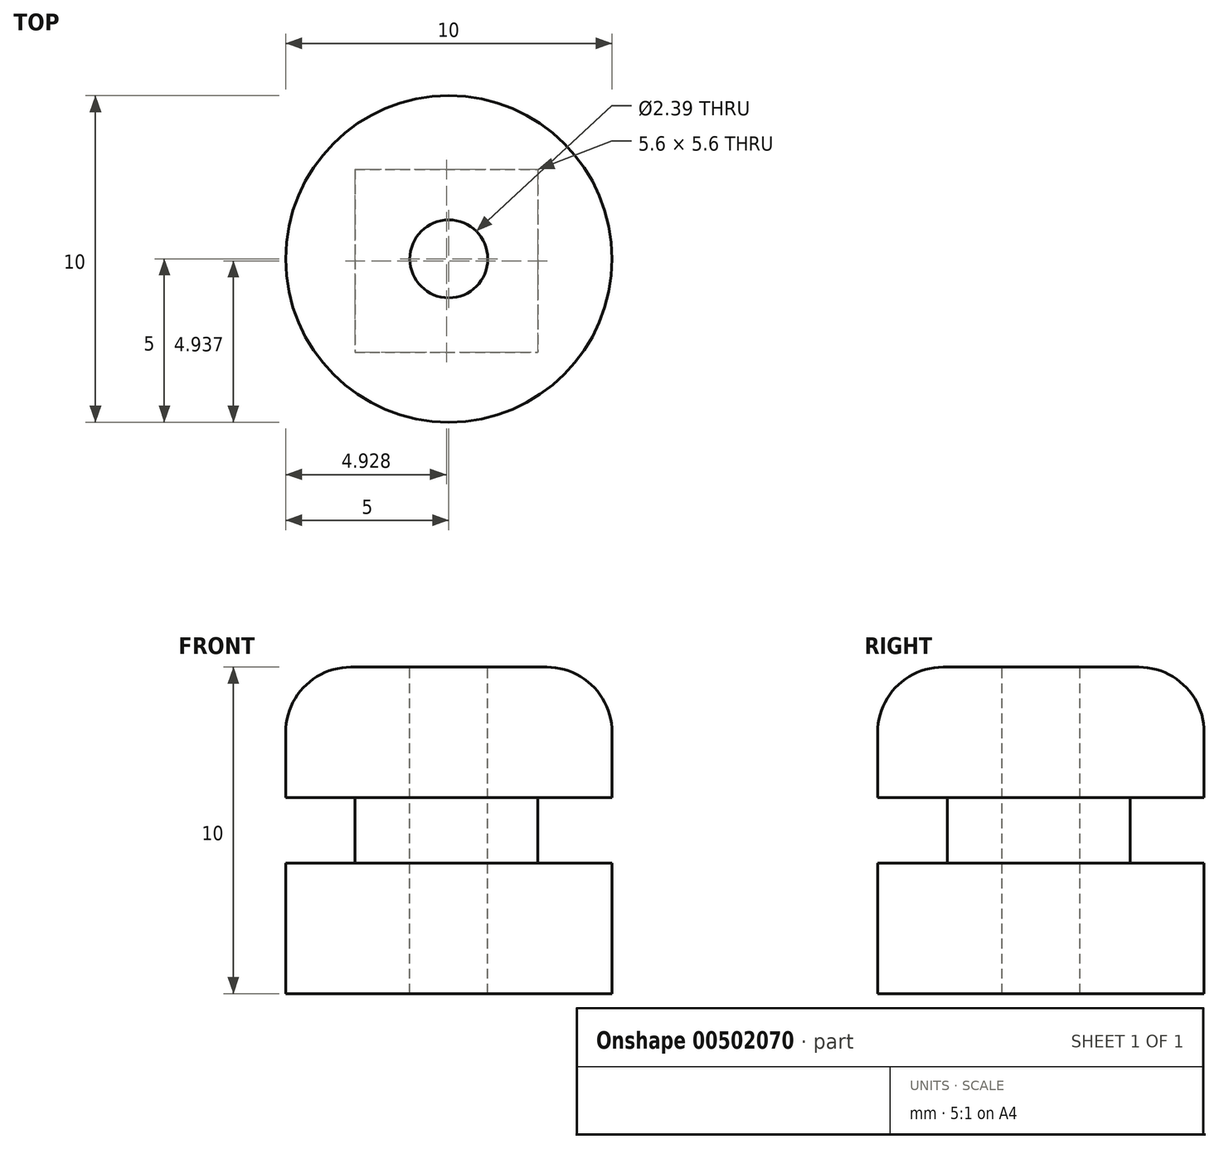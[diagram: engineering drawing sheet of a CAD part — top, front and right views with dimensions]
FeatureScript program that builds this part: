
annotation { "Feature Type Name" : "Feature", "Feature Type Description" : "" }
export const myFeature = defineFeature(function(context is Context, id is Id, definition is map)
    precondition{}
    {
        {
            var Q0;
            Q0=qCreatedBy(makeId("Top.planeOp"),FACE);
            var sketch = newSketch(context, id + "F0", { "sketchPlane" : qUnion([Q0])});
            skCircle(sketch, "E0", {"center": v(0, 0) * mm, "radius": 5 * mm});
            skSolve(sketch);
        }
        {
            var Q0;
            Q0 = qSketchRegion(id + "F0", true);
            extrude(context, id + "F1", {"entities" : qUnion([Q0]), "depth" : 4 * mm});
        }
        {
            var Q0;
            Q0=makeQuery(id+"F1.opExtrude","CAP_FACE",FACE,{"disambiguationData":[OSD([sQuery(id+"F0.wireOp",EDGE,"E0")])],"isStart":false});
            var sketch = newSketch(context, id + "F2", { "sketchPlane" : qUnion([Q0])});
            skLineSegment(sketch, "E1.bottom", {"start": v(-2.87, 2.74) * mm, "end": v(2.73, 2.74) * mm});
            skLineSegment(sketch, "E1.top", {"start": v(-2.87, -2.86) * mm, "end": v(2.73, -2.86) * mm});
            skLineSegment(sketch, "E1.left", {"start": v(-2.87, 2.74) * mm, "end": v(-2.87, -2.86) * mm});
            skLineSegment(sketch, "E1.right", {"start": v(2.73, 2.74) * mm, "end": v(2.73, -2.86) * mm});
            skSolve(sketch);
        }
        {
            var Q0;
            Q0 = qSketchRegion(id + "F2", true);
            extrude(context, id + "F3", {"entities" : qUnion([Q0]), "operationType" : NewBodyOperationType.ADD, "depth" : 2 * mm});
        }
        {
            var Q0;
            Q0=makeQuery(id+"F3.opExtrude","CAP_FACE",FACE,{"disambiguationData":[OSD([sQuery(id+"F2.wireOp",EDGE,"E1.bottom"),sQuery(id+"F2.wireOp",EDGE,"E1.top"),sQuery(id+"F2.wireOp",EDGE,"E1.left"),sQuery(id+"F2.wireOp",EDGE,"E1.right")])],"isStart":false});
            var sketch = newSketch(context, id + "F4", { "sketchPlane" : qUnion([Q0])});
            skCircle(sketch, "E2", {"center": v(0, 0) * mm, "radius": 5 * mm});
            skSolve(sketch);
        }
        {
            var Q0;
            Q0 = qSketchRegion(id + "F4", true);
            extrude(context, id + "F5", {"entities" : qUnion([Q0]), "operationType" : NewBodyOperationType.ADD, "depth" : 4 * mm});
        }
        {
            var Q0;
            Q0=makeQuery(id+"F5.opExtrude","CAP_FACE",FACE,{"disambiguationData":[OSD([sQuery(id+"F4.wireOp",EDGE,"E2")])],"isStart":false});
            var sketch = newSketch(context, id + "F6", { "sketchPlane" : qUnion([Q0])});
            skCircle(sketch, "E3", {"center": v(0, 0) * mm, "radius": 1.2 * mm});
            skSolve(sketch);
        }
        {
            var Q0;
            Q0 = qSketchRegion(id + "F6", true);
            extrude(context, id + "F7", {"entities" : qUnion([Q0]), "operationType" : NewBodyOperationType.REMOVE, "endBound" : BoundingType.THROUGH_ALL, "oppositeDirection" : true, "depth" : 25 * mm});
        }
        {
            var Q0;
            Q0=makeQuery(id+"F5.opExtrude","CAP_EDGE",EDGE,{"disambiguationData":[OSD([sQuery(id+"F4.wireOp",EDGE,"E2")])],"isStart":false});
            fillet(context, id + "F8", {"entities" : qUnion([Q0]), "radius" : 2 * mm, "tangentPropagation" : true, "allowEdgeOverflow" : false});
        }
    });
